# Revit family: Accessory-Robe_Hook-KOHLER-Forte-K-11375
name_source: partatom
category: Generic Models
revit_build: Autodesk Revit 2015 (Build: 20140606_1530(x64)
units: mm (PartAtom-declared; Revit-internal decimal feet)

## types (3) — shared parameters
ADA Compliant = Yes
Assembly Code = C1030200
Cold Water Diameter = 0"
Date Modified = 09/15/2017
Default Elevation = 42"
Description = Sculpted double robe hook
Height = 2 17/32"
Length = 2 13/16"
Manufacturer = Kohler
MasterFormat 1995 = 10820
MasterFormat 2004 = 10.28.13
Material = Premium metal construction
Product Documentation Link = http://www.us.kohler.com
Product Name = Forté
Product Page URL = http://www.us.kohler.com
URL = http://www.us.kohler.com
Waste Connection Diameter = 0"
Width = 2 17/32"

## per-type parameters (varying)
| type | Finish | Model | Type |
| CP-Polished Chrome | Metal-Kohler-CP-Polished Chrome | K-11375-CP | 1 |
| G-Brushed Chrome | Metal-Kohler-G-Brushed Chrome | K-11375-G | 2 |
| BN-Vibrant Brushed Nickel | Metal-Kohler-BN-Vibrant Brushed Nickel | K-11375-BN | 3 |

## geometry (parser evidence)
native form markers: Sweep x5
no freeform markers — native parametric forms only
